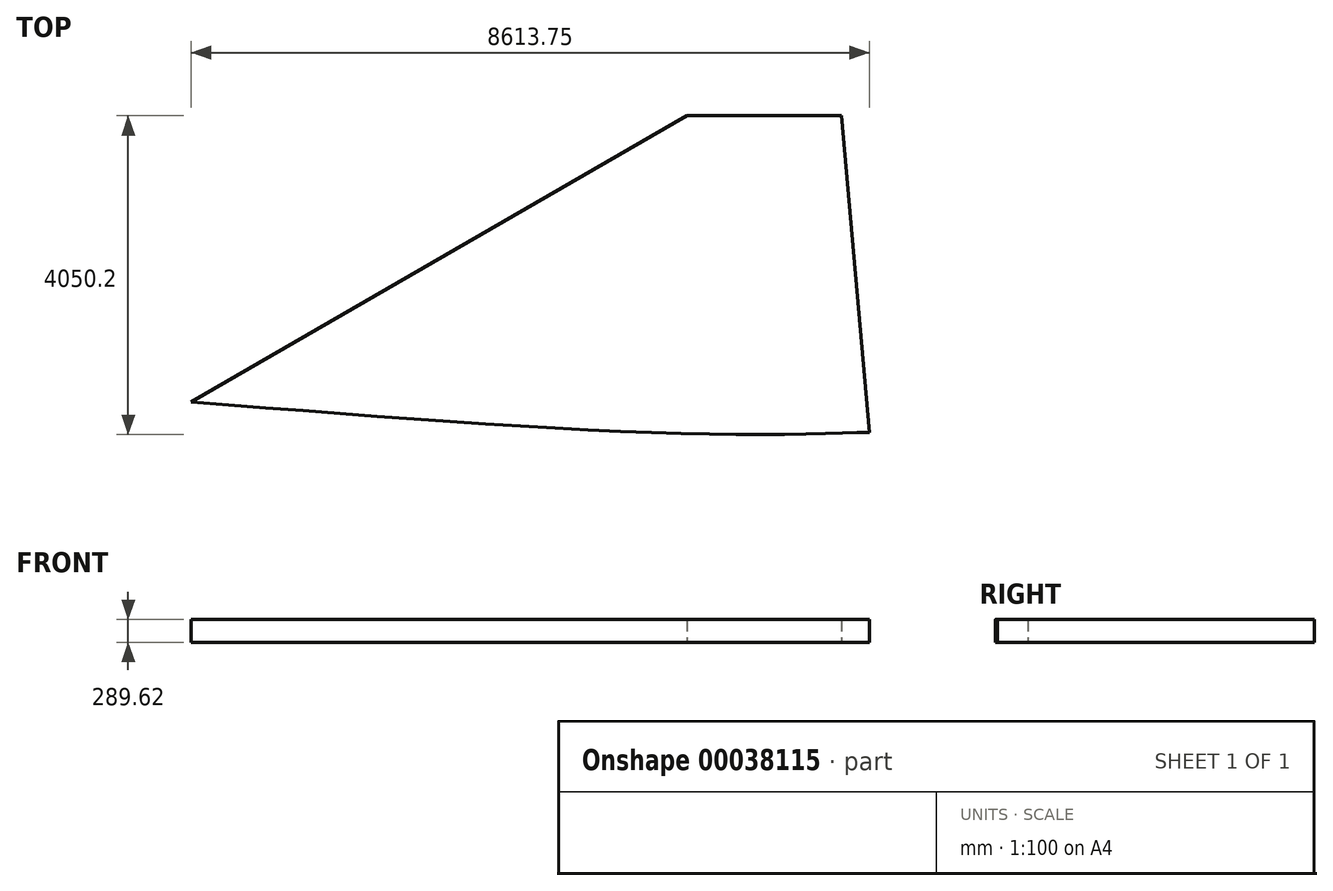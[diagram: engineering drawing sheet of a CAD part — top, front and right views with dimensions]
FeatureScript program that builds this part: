
annotation { "Feature Type Name" : "Feature", "Feature Type Description" : "" }
export const myFeature = defineFeature(function(context is Context, id is Id, definition is map)
    precondition{}
    {
        {
            var Q0;
            Q0=qCreatedBy(makeId("Top.planeOp"),FACE);
            var sketch = newSketch(context, id + "F0", { "sketchPlane" : qUnion([Q0])});
            skLineSegment(sketch, "E0", {"start": v(0, 0) * mm, "end": v(10107.64, 5835.65) * mm});
            skLineSegment(sketch, "E1", {"start": v(10861.04, 0) * mm, "end": v(0, 0) * mm});
            skLineSegment(sketch, "E2", {"start": v(10107.64, 5835.65) * mm, "end": v(10350.49, 5835.65) * mm});
            skLineSegment(sketch, "E3", {"start": v(10861.04, 0) * mm, "end": v(10350.49, 5835.65) * mm});
            skSolve(sketch);
        }
        {
            var Q0;
            Q0=makeQuery(id+"F0.imprint","IMPRINT",FACE,{"disambiguationData":[TD([[makeQuery(id+"F0.imprint","IMPRINT",EDGE,{"derivedFrom":sQuery(id+"F0.wireOp",EDGE,"E0")}),-1.0]])]});
            var sketch = newSketch(context, id + "F1", { "sketchPlane" : qUnion([Q0])});
            skLineSegment(sketch, "E4", {"start": v(2171.45, 2095.8) * mm, "end": v(2171.45, -777.95) * mm, "construction": true});
            skLineSegment(sketch, "E5", {"start": v(10861.04, 1272.68) * mm, "end": v(10861.04, -670.62) * mm, "construction": true});
            skFitSpline(sketch, "E6", {"points": [v(2171.45, 1253.68) * mm, v(8810.75, 843.79) * mm, v(10861.04, 867.4) * mm], "startDerivative": vector(11078.91, -881.61) * mm, "endDerivative": vector(2816.68, 0) * mm});
            skLineSegment(sketch, "E7", {"start": v(2171.45, 1253.68) * mm, "end": v(10107.64, 5835.65) * mm});
            skLineSegment(sketch, "E8", {"start": v(10107.64, 5835.65) * mm, "end": v(10350.49, 5835.65) * mm});
            skLineSegment(sketch, "E9", {"start": v(10350.49, 5835.65) * mm, "end": v(10785.2, 866.89) * mm});
            skSolve(sketch);
        }
        {
            var Q0;
            Q0=qSketchRegion(id+"F1",true);
            extrude(context, id + "F2", {"entities" : qUnion([Q0]), "depth" : 289.62 * mm});
        }
        {
            var Q0;
            Q0=makeQuery(id+"F2.opExtrude","CAP_FACE",FACE,{"disambiguationData":[OSD([sQuery(id+"F1.wireOp",EDGE,"E6"),sQuery(id+"F1.wireOp",EDGE,"E7"),sQuery(id+"F1.wireOp",EDGE,"E8"),sQuery(id+"F1.wireOp",EDGE,"E9")])],"isStart":false});
            var sketch = newSketch(context, id + "F3", { "sketchPlane" : qUnion([Q0])});
            skLineSegment(sketch, "E10.bottom", {"start": v(11012.82, 5835.65) * mm, "end": v(8403.66, 5835.65) * mm});
            skLineSegment(sketch, "E10.top", {"start": v(11012.82, 4890.77) * mm, "end": v(8403.66, 4890.77) * mm});
            skLineSegment(sketch, "E10.left", {"start": v(11012.82, 5835.65) * mm, "end": v(11012.82, 4890.77) * mm});
            skLineSegment(sketch, "E10.right", {"start": v(8403.66, 5835.65) * mm, "end": v(8403.66, 4890.77) * mm});
            skSolve(sketch);
        }
        {
            var Q0;
            Q0=qSketchRegion(id+"F3",true);
            extrude(context, id + "F4", {"entities" : qUnion([Q0]), "operationType" : NewBodyOperationType.REMOVE, "endBound" : BoundingType.THROUGH_ALL, "oppositeDirection" : true, "depth" : 25.4 * mm});
        }
    });
